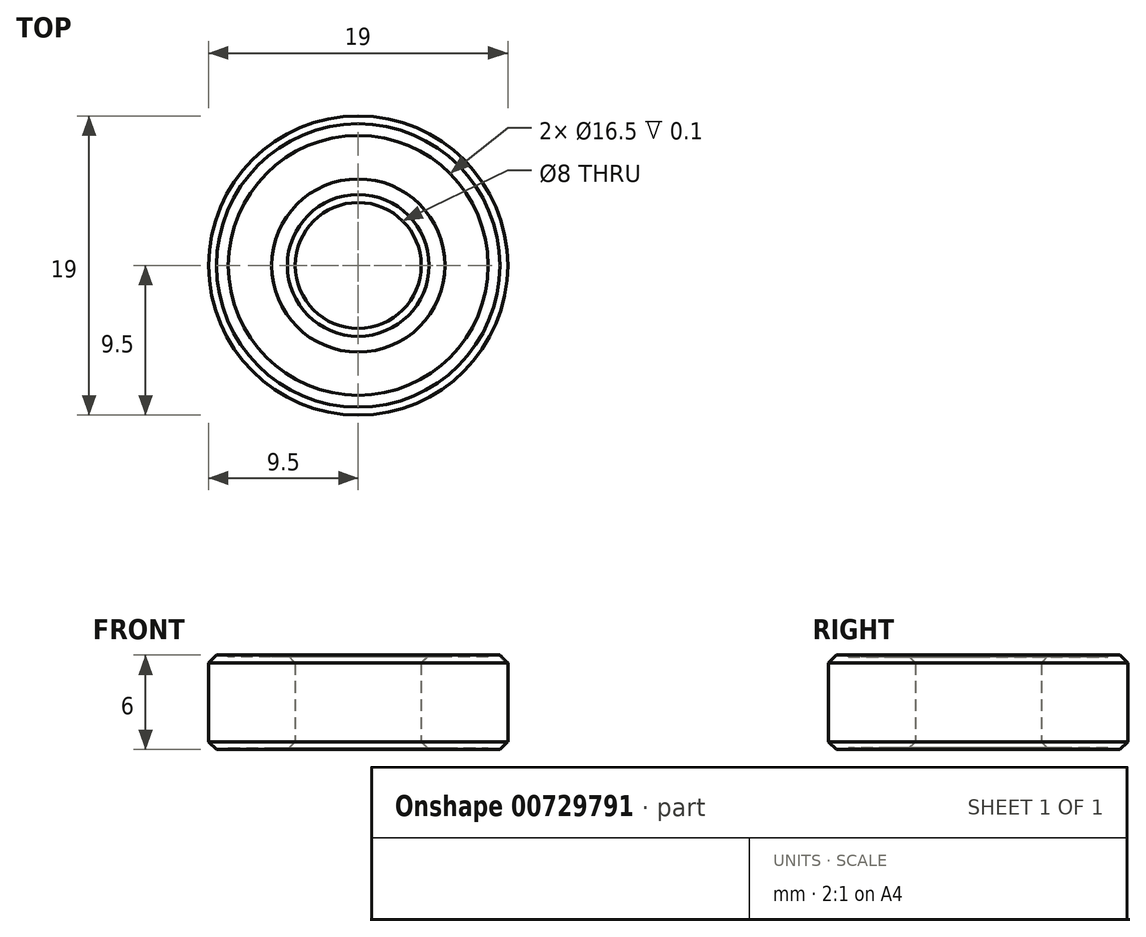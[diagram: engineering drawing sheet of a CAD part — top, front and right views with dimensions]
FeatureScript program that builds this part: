
annotation { "Feature Type Name" : "Feature", "Feature Type Description" : "" }
export const myFeature = defineFeature(function(context is Context, id is Id, definition is map)
    precondition{}
    {
        {
            var Q0;
            Q0=qCreatedBy(makeId("Top.planeOp"),FACE);
            var sketch = newSketch(context, id + "F0", { "sketchPlane" : qUnion([Q0])});
            skCircle(sketch, "E0", {"center": v(0, 0) * mm, "radius": 9.5 * mm});
            skCircle(sketch, "E1", {"center": v(0, 0) * mm, "radius": 4 * mm});
            skSolve(sketch);
        }
        {
            var Q0;
            Q0=makeQuery(id+"F0.imprint","IMPRINT",FACE,{"disambiguationData":[TD([[makeQuery(id+"F0.imprint","IMPRINT",EDGE,{"derivedFrom":sQuery(id+"F0.wireOp",EDGE,"E0")}),1.0]])]});
            extrude(context, id + "F1", {"entities" : qUnion([Q0]), "endBound" : BoundingType.SYMMETRIC, "depth" : 6 * mm, "offsetDistance" : 25 * mm});
        }
        {
            var Q0;
            Q0=makeQuery(id+"F1.opExtrude","CAP_FACE",FACE,{"disambiguationData":[OSD([sQuery(id+"F0.wireOp",EDGE,"E0"),sQuery(id+"F0.wireOp",EDGE,"E1")])],"isStart":false});
            var Q1;
            Q1=makeQuery(id+"F1.opExtrude","CAP_FACE",FACE,{"disambiguationData":[OSD([sQuery(id+"F0.wireOp",EDGE,"E0"),sQuery(id+"F0.wireOp",EDGE,"E1")])],"isStart":true});
            chamfer(context, id + "F2", {"entities" : qUnion([Q0, Q1]), "width" : 0.5 * mm, "tangentPropagation" : true});
        }
        {
            var Q0;
            Q0=makeQuery(id+"F1.opExtrude","CAP_FACE",FACE,{"disambiguationData":[OSD([sQuery(id+"F0.wireOp",EDGE,"E0"),sQuery(id+"F0.wireOp",EDGE,"E1")])],"isStart":false});
            var sketch = newSketch(context, id + "F3", { "sketchPlane" : qUnion([Q0])});
            skCircle(sketch, "E2", {"center": v(0, 0) * mm, "radius": 5.5 * mm});
            skCircle(sketch, "E3", {"center": v(0, 0) * mm, "radius": 8.25 * mm});
            skSolve(sketch);
        }
        {
            var Q0;
            Q0 = qSketchRegion(id + "F3", true);
            extrude(context, id + "F4", {"entities" : qUnion([Q0]), "operationType" : NewBodyOperationType.REMOVE, "oppositeDirection" : true, "depth" : 0.1 * mm, "offsetDistance" : 25 * mm});
        }
        {
            var Q0;
            Q0=makeQuery(id+"F1.opExtrude","CAP_FACE",FACE,{"disambiguationData":[OSD([sQuery(id+"F0.wireOp",EDGE,"E0"),sQuery(id+"F0.wireOp",EDGE,"E1")])],"isStart":true});
            var sketch = newSketch(context, id + "F5", { "sketchPlane" : qUnion([Q0])});
            skCircle(sketch, "E4.0", {"center": v(0, 0) * mm, "radius": 8.25 * mm});
            skCircle(sketch, "E5.0", {"center": v(0, 0) * mm, "radius": 5.5 * mm});
            skSolve(sketch);
        }
        {
            var Q0;
            Q0 = qSketchRegion(id + "F5", true);
            extrude(context, id + "F6", {"entities" : qUnion([Q0]), "operationType" : NewBodyOperationType.REMOVE, "oppositeDirection" : true, "depth" : 0.1 * mm, "offsetDistance" : 25 * mm});
        }
    });
